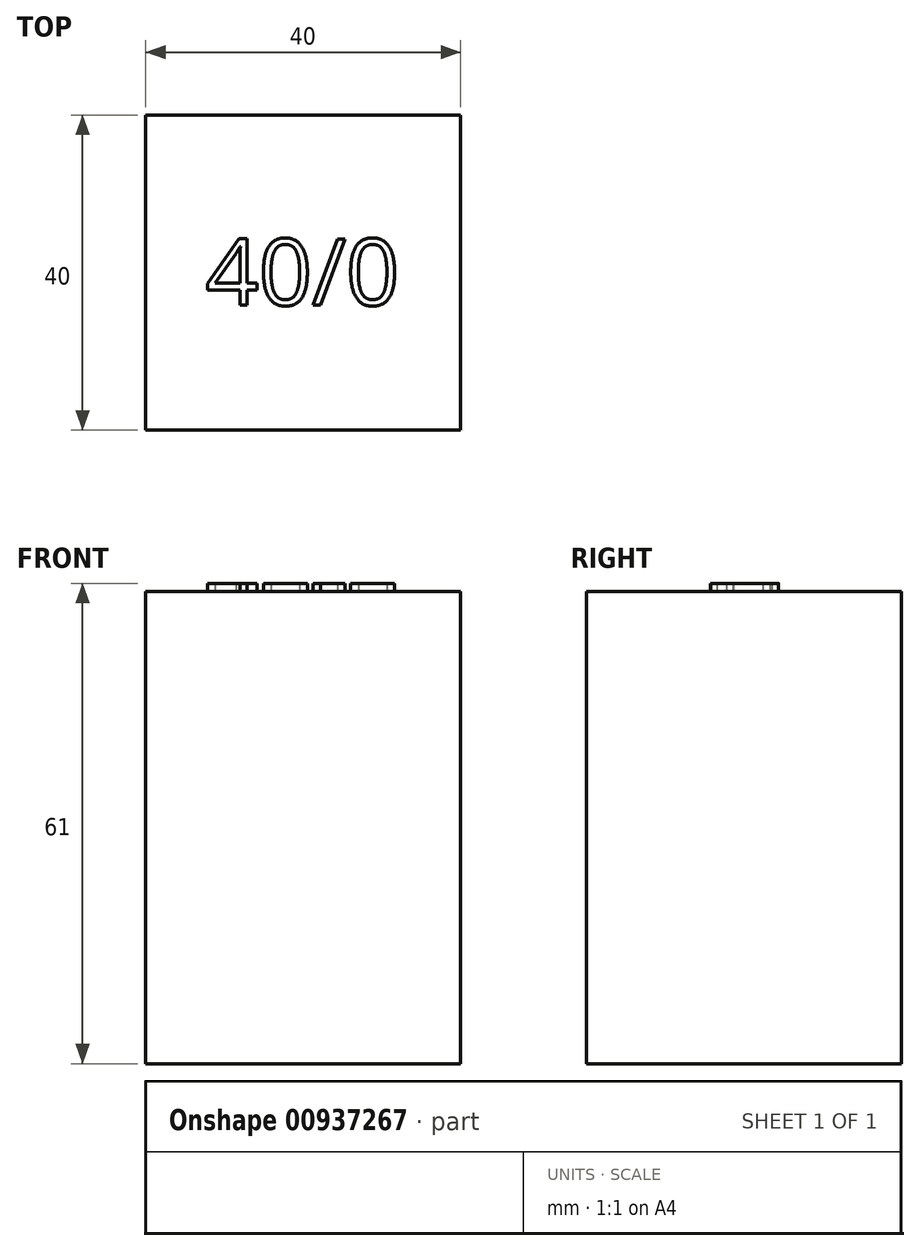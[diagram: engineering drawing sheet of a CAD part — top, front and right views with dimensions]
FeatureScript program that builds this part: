
annotation { "Feature Type Name" : "Feature", "Feature Type Description" : "" }
export const myFeature = defineFeature(function(context is Context, id is Id, definition is map)
    precondition{}
    {
        {
            var Q0;
            Q0=qCreatedBy(makeId("Top.planeOp"),FACE);
            var sketch = newSketch(context, id + "F0", { "sketchPlane" : qUnion([Q0])});
            skLineSegment(sketch, "E0.bottom", {"start": v(-20, 20) * mm, "end": v(20, 20) * mm});
            skLineSegment(sketch, "E0.top", {"start": v(-20, -20) * mm, "end": v(20, -20) * mm});
            skLineSegment(sketch, "E0.left", {"start": v(-20, 20) * mm, "end": v(-20, -20) * mm});
            skLineSegment(sketch, "E0.right", {"start": v(20, 20) * mm, "end": v(20, -20) * mm});
            skPoint(sketch, "E0.middle", {"position": v(0, 0) * mm});
            skSolve(sketch);
        }
        {
            var Q0;
            Q0=makeQuery(id+"F0.imprint","IMPRINT",FACE,{"disambiguationData":[TD([[makeQuery(id+"F0.imprint","IMPRINT",EDGE,{"derivedFrom":sQuery(id+"F0.wireOp",EDGE,"E0.bottom")}),-1.0]])]});
            extrude(context, id + "F1", {"entities" : qUnion([Q0]), "depth" : 60 * mm, "offsetDistance" : 25 * mm});
        }
        {
            var Q0;
            Q0=makeQuery(id+"F1.opExtrude","CAP_FACE",FACE,{"disambiguationData":[OSD([sQuery(id+"F0.wireOp",EDGE,"E0.bottom"),sQuery(id+"F0.wireOp",EDGE,"E0.top"),sQuery(id+"F0.wireOp",EDGE,"E0.left"),sQuery(id+"F0.wireOp",EDGE,"E0.right")])],"isStart":false});
            var sketch = newSketch(context, id + "F2", { "sketchPlane" : qUnion([Q0])});
            skText(sketch, "E1", { "text": "40/0", "fontName": "OpenSans-Regular.ttf"});
            const initialGuessF2  = {"E1": [-0.01238, -0.00416, 1, 0, 0.0085]};
            skSetInitialGuess(sketch, initialGuessF2);
            skSolve(sketch);
        }
        {
            var Q0;
            Q0 = qSketchRegion(id + "F2", true);
            extrude(context, id + "F3", {"entities" : qUnion([Q0]), "operationType" : NewBodyOperationType.ADD, "depth" : 1 * mm, "offsetDistance" : 25 * mm});
        }
    });
